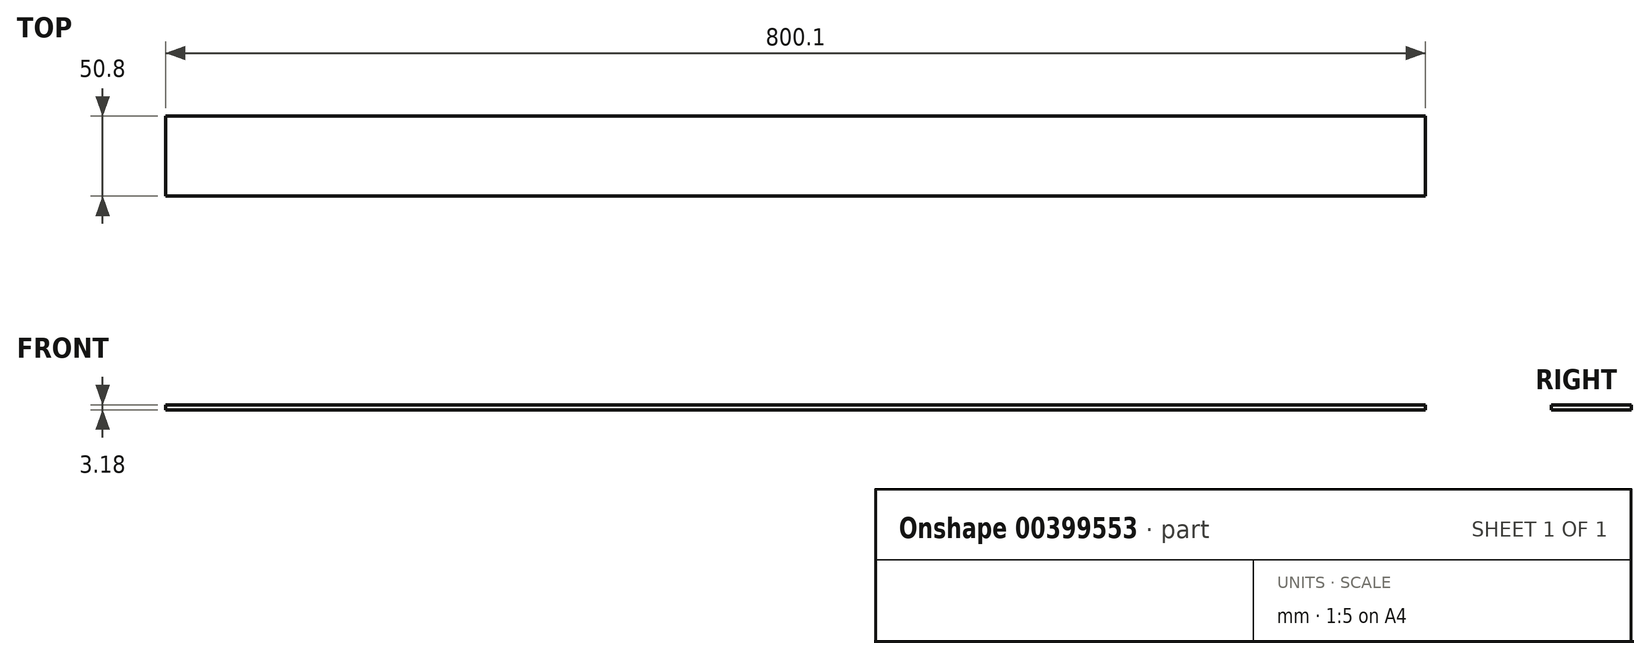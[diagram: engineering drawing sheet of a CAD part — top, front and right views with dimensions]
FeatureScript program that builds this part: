
annotation { "Feature Type Name" : "Feature", "Feature Type Description" : "" }
export const myFeature = defineFeature(function(context is Context, id is Id, definition is map)
    precondition{}
    {
        {
            var Q0;
            Q0=qCreatedBy(makeId("Right.planeOp"),FACE);
            var sketch = newSketch(context, id + "F0", { "sketchPlane" : qUnion([Q0])});
            skLineSegment(sketch, "E0.bottom", {"start": v(25.4, 1.59) * mm, "end": v(-25.4, 1.59) * mm});
            skLineSegment(sketch, "E0.top", {"start": v(25.4, -1.59) * mm, "end": v(-25.4, -1.59) * mm});
            skLineSegment(sketch, "E0.left", {"start": v(25.4, 1.59) * mm, "end": v(25.4, -1.59) * mm});
            skLineSegment(sketch, "E0.right", {"start": v(-25.4, 1.59) * mm, "end": v(-25.4, -1.59) * mm});
            skPoint(sketch, "E0.middle", {"position": v(0, 0) * mm});
            skSolve(sketch);
        }
        {
            var Q0;
            Q0=makeQuery(id+"F0.imprint","IMPRINT",FACE,{"disambiguationData":[TD([[makeQuery(id+"F0.imprint","IMPRINT",EDGE,{"derivedFrom":sQuery(id+"F0.wireOp",EDGE,"E0.bottom")}),1.0]])]});
            extrude(context, id + "F1", {"entities" : qUnion([Q0]), "endBound" : BoundingType.SYMMETRIC, "depth" : 800.1 * mm});
        }
    });
